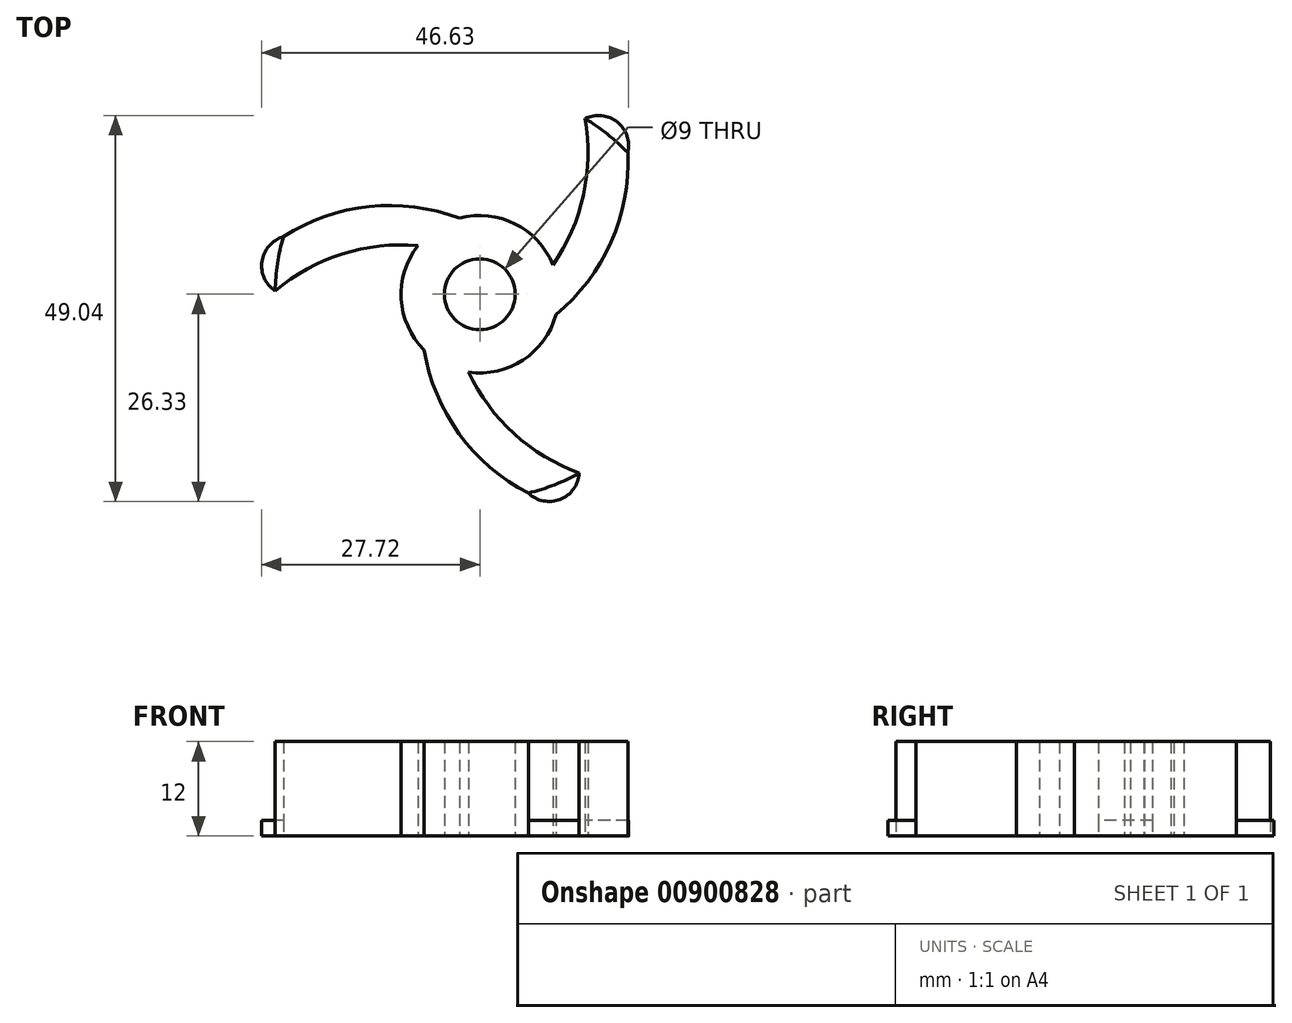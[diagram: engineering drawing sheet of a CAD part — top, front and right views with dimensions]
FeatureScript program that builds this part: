
annotation { "Feature Type Name" : "Feature", "Feature Type Description" : "" }
export const myFeature = defineFeature(function(context is Context, id is Id, definition is map)
    precondition{}
    {
        {
            var Q0;
            Q0=qCreatedBy(makeId("Top.planeOp"),FACE);
            var sketch = newSketch(context, id + "F0", { "sketchPlane" : qUnion([Q0])});
            skCircle(sketch, "E0", {"center": v(0, 0) * mm, "radius": 4.5 * mm});
            skCircle(sketch, "E1", {"center": v(0, 0) * mm, "radius": 10 * mm});
            skArc(sketch, "E2.trimOffspring", {"start": v(-2.6, 9.66) * mm, "mid": v(-14.06, 11.13) * mm, "end": v(-24.96, 7.3) * mm});
            skArc(sketch, "E3.trimOffspring", {"start": v(-7.86, 6.18) * mm, "mid": v(-17.5, 5.1) * mm, "end": v(-26, 0.42) * mm});
            skArc(sketch, "E4.1.0", {"start": v(-7.06, -7.08) * mm, "mid": v(-2.61, -17.74) * mm, "end": v(6.16, -25.26) * mm});
            skArc(sketch, "E4.1.1", {"start": v(-1.43, -9.9) * mm, "mid": v(4.33, -17.7) * mm, "end": v(12.63, -22.73) * mm});
            skArc(sketch, "E4.2.0", {"start": v(9.66, -2.58) * mm, "mid": v(16.67, 6.6) * mm, "end": v(18.8, 17.96) * mm});
            skArc(sketch, "E4.2.1", {"start": v(9.28, 3.71) * mm, "mid": v(13.16, 12.6) * mm, "end": v(13.37, 22.3) * mm});
            skArc(sketch, "E5", {"start": v(-24.96, 7.3) * mm, "mid": v(-25.7, 3.9) * mm, "end": v(-26, 0.42) * mm});
            skArc(sketch, "E6.trimOffspring", {"start": v(18.8, 17.96) * mm, "mid": v(16.23, 20.32) * mm, "end": v(13.37, 22.3) * mm});
            skArc(sketch, "E7.trimOffspring", {"start": v(6.16, -25.26) * mm, "mid": v(9.48, -24.2) * mm, "end": v(12.63, -22.73) * mm});
            skPoint(sketch, "E8.orphan", {"position": v(-26.85, 5.95) * mm});
            skPoint(sketch, "E9.orphan", {"position": v(-27.48, -0.93) * mm});
            skPoint(sketch, "E10.orphan", {"position": v(12.94, 24.27) * mm});
            skPoint(sketch, "E11.orphan", {"position": v(18.58, 20.28) * mm});
            skPoint(sketch, "E12.orphan", {"position": v(14.55, -23.34) * mm});
            skPoint(sketch, "E13.orphan", {"position": v(8.27, -26.23) * mm});
            skArc(sketch, "E14", {"start": v(-24.96, 7.3) * mm, "mid": v(-27.67, 4.2) * mm, "end": v(-26, 0.42) * mm});
            skArc(sketch, "E15.1.0", {"start": v(6.16, -25.26) * mm, "mid": v(10.2, -26.06) * mm, "end": v(12.63, -22.73) * mm});
            skArc(sketch, "E15.2.0", {"start": v(18.8, 17.96) * mm, "mid": v(17.47, 21.87) * mm, "end": v(13.37, 22.3) * mm});
            skSolve(sketch);
        }
        {
            var Q0;
            {var subQ0=sQuery(id+"F0.wireOp",EDGE,"E2.trimOffspring");Q0=makeQuery(id+"F0.imprint","IMPRINT",FACE,{"disambiguationData":[TD([[makeQuery(id+"F0.imprint","IMPRINT",EDGE,{"derivedFrom":subQ0}),1.0]])]});}
            var Q1;
            {var subQ0=sQuery(id+"F0.wireOp",EDGE,"E4.2.0");Q1=makeQuery(id+"F0.imprint","IMPRINT",FACE,{"disambiguationData":[TD([[makeQuery(id+"F0.imprint","IMPRINT",EDGE,{"derivedFrom":subQ0}),1.0]])]});}
            var Q2;
            Q2=makeQuery(id+"F0.imprint","IMPRINT",FACE,{"disambiguationData":[TD([[makeQuery(id+"F0.imprint","IMPRINT",EDGE,{"derivedFrom":sQuery(id+"F0.wireOp",EDGE,"E0")}),-1.0]])]});
            var Q3;
            {var subQ0=sQuery(id+"F0.wireOp",EDGE,"E4.1.0");Q3=makeQuery(id+"F0.imprint","IMPRINT",FACE,{"disambiguationData":[TD([[makeQuery(id+"F0.imprint","IMPRINT",EDGE,{"derivedFrom":subQ0}),1.0]])]});}
            extrude(context, id + "F1", {"entities" : qUnion([Q0, Q1, Q2, Q3]), "depth" : 12 * mm, "offsetDistance" : 25 * mm});
        }
        {
            var Q0;
            Q0=makeQuery(id+"F0.imprint","IMPRINT",FACE,{"disambiguationData":[TD([[makeQuery(id+"F0.imprint","IMPRINT",EDGE,{"derivedFrom":sQuery(id+"F0.wireOp",EDGE,"E5")}),-1.0]])]});
            var Q1;
            Q1=makeQuery(id+"F0.imprint","IMPRINT",FACE,{"disambiguationData":[TD([[makeQuery(id+"F0.imprint","IMPRINT",EDGE,{"derivedFrom":sQuery(id+"F0.wireOp",EDGE,"E7.trimOffspring")}),-1.0]])]});
            var Q2;
            Q2=makeQuery(id+"F0.imprint","IMPRINT",FACE,{"disambiguationData":[TD([[makeQuery(id+"F0.imprint","IMPRINT",EDGE,{"derivedFrom":sQuery(id+"F0.wireOp",EDGE,"E6.trimOffspring")}),-1.0]])]});
            extrude(context, id + "F2", {"entities" : qUnion([Q0, Q1, Q2]), "operationType" : NewBodyOperationType.ADD, "depth" : 2 * mm, "offsetDistance" : 25 * mm});
        }
    });
